# Revit family: REYE-2 NDWSxxxRA
name_source: partatom
category: Leuchten
units: mm (PartAtom-declared; Revit-internal decimal feet)

## family parameters
Basisbauteil = Fläche
Beim Laden mit Abzugskörper schneiden = Nein
Bemaßung runder Anschluss = Durchmesser verwenden
Gemeinsam genutzt = Nein
Lichtquelle = Ja
OmniClass-Nummer = 23.80.70.11
OmniClass-Titel = Luminaries for Internal Lighting
Raumberechnungspunkt = Nein
Teiletyp = Normal

## types (6) — shared parameters
Baugruppenkennzeichen = D5020200
Datei für fotometrisches Netz = REYE-2 DAWS840RA1300.IES
Emissionsform beim Rendern sichtbar = Nein
Farbfilter = 16777215
Farbtemperaturverschiebung bei Dämpfen der Lampe = <Keine Auswahl>
Hersteller = RIDI Leuchten GmbH
Lampe = LED
Neigungswinkel = 90.00°
Scheinlast = 102 VA
URL = www.ridi.de
Von Breite des Rechtecks ausssenden = 208 mm
Von Länge des Rechtecks aussenden = 182 mm  [stored 0.597113 ft]
brand = RIDI
conformity mark = CE
electrical safety class = 1
height = 74 mm  [stored 0.242782 ft]
ingress protection (IP) code = IP20
length = 299 mm  [stored 0.980971 ft]
nominal frequency = 50-60Hz
nominal voltage = 230
rated input power = 102
voltage type (AC, DC, UC) = AC
weight = 3.2
width = 199 mm  [stored 0.652887 ft]
zero-valued in all types: Vorgabe-Ansicht

## per-type parameters (varying)
| type | Modell |
| REYE-2 NDWS830RA1300 | 0322047 |
| REYE-2 DAWS830RA1300 | 0332047 |
| REYE-2 NDWS840RA1300 | 0322048 |
| REYE-2 DAWS840RA1300 | 0332048 |
| REYE-2 NDWS930RA1100 | 0322049 |
| REYE-2 DAWS930RA1100 | 0332049 |

note: column(s) folded — value = type name in every type: product name

note: [stored X ft] marks values corroborated as IEEE doubles in the binary element streams (Revit-internal decimal feet)
